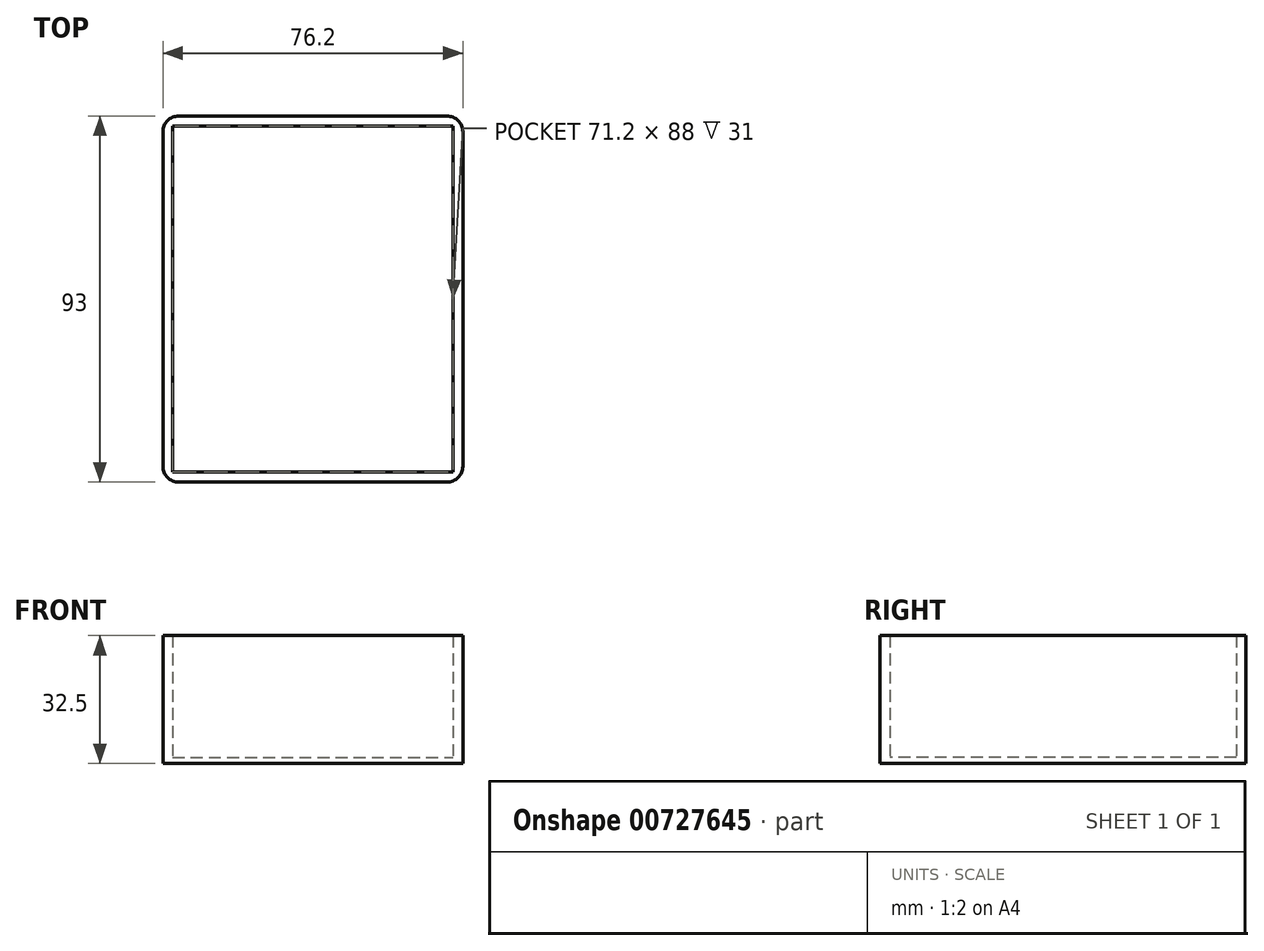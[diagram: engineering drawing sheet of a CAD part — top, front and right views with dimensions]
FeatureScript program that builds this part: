
annotation { "Feature Type Name" : "Feature", "Feature Type Description" : "" }
export const myFeature = defineFeature(function(context is Context, id is Id, definition is map)
    precondition{}
    {
        {
            var Q0;
            Q0=qCreatedBy(makeId("Top.planeOp"),FACE);
            var sketch = newSketch(context, id + "F0", { "sketchPlane" : qUnion([Q0])});
            skLineSegment(sketch, "E0", {"start": v(-31.2, 4) * mm, "end": v(37, 4) * mm});
            skLineSegment(sketch, "E1", {"start": v(-35.2, 0) * mm, "end": v(-35.2, -85) * mm});
            skLineSegment(sketch, "E2", {"start": v(-31.2, -89) * mm, "end": v(37, -89) * mm});
            skLineSegment(sketch, "E3", {"start": v(41, -85) * mm, "end": v(41, 0) * mm});
            skArc(sketch, "E4", {"start": v(41, 0) * mm, "mid": v(39.83, 2.83) * mm, "end": v(37, 4) * mm});
            skArc(sketch, "E5", {"start": v(-31.2, 4) * mm, "mid": v(-34.03, 2.83) * mm, "end": v(-35.2, 0) * mm});
            skArc(sketch, "E6", {"start": v(-35.2, -85) * mm, "mid": v(-34.03, -87.83) * mm, "end": v(-31.2, -89) * mm});
            skArc(sketch, "E7", {"start": v(41, -85) * mm, "mid": v(39.83, -87.83) * mm, "end": v(37, -89) * mm});
            skLineSegment(sketch, "E8", {"start": v(38.5, 1.5) * mm, "end": v(38.5, -86.5) * mm});
            skLineSegment(sketch, "E9", {"start": v(-32.7, -86.5) * mm, "end": v(38.5, -86.5) * mm});
            skLineSegment(sketch, "E10", {"start": v(-32.7, 1.5) * mm, "end": v(-32.7, -86.5) * mm});
            skLineSegment(sketch, "E11", {"start": v(-32.7, 1.5) * mm, "end": v(38.5, 1.5) * mm});
            skSolve(sketch);
        }
        {
            var Q0;
            Q0=makeQuery(id+"F0.imprint","IMPRINT",FACE,{"disambiguationData":[TD([[makeQuery(id+"F0.imprint","IMPRINT",EDGE,{"derivedFrom":sQuery(id+"F0.wireOp",EDGE,"E0")}),-1.0]])]});
            extrude(context, id + "F1", {"entities" : qUnion([Q0]), "depth" : 32.5 * mm, "offsetDistance" : 25 * mm});
        }
        {
            var Q0;
            Q0=makeQuery(id+"F0.imprint","IMPRINT",FACE,{"disambiguationData":[TD([[makeQuery(id+"F0.imprint","IMPRINT",EDGE,{"derivedFrom":sQuery(id+"F0.wireOp",EDGE,"E8")}),-1.0]])]});
            extrude(context, id + "F2", {"entities" : qUnion([Q0]), "operationType" : NewBodyOperationType.ADD, "depth" : 1.5 * mm, "offsetDistance" : 25 * mm});
        }
    });
